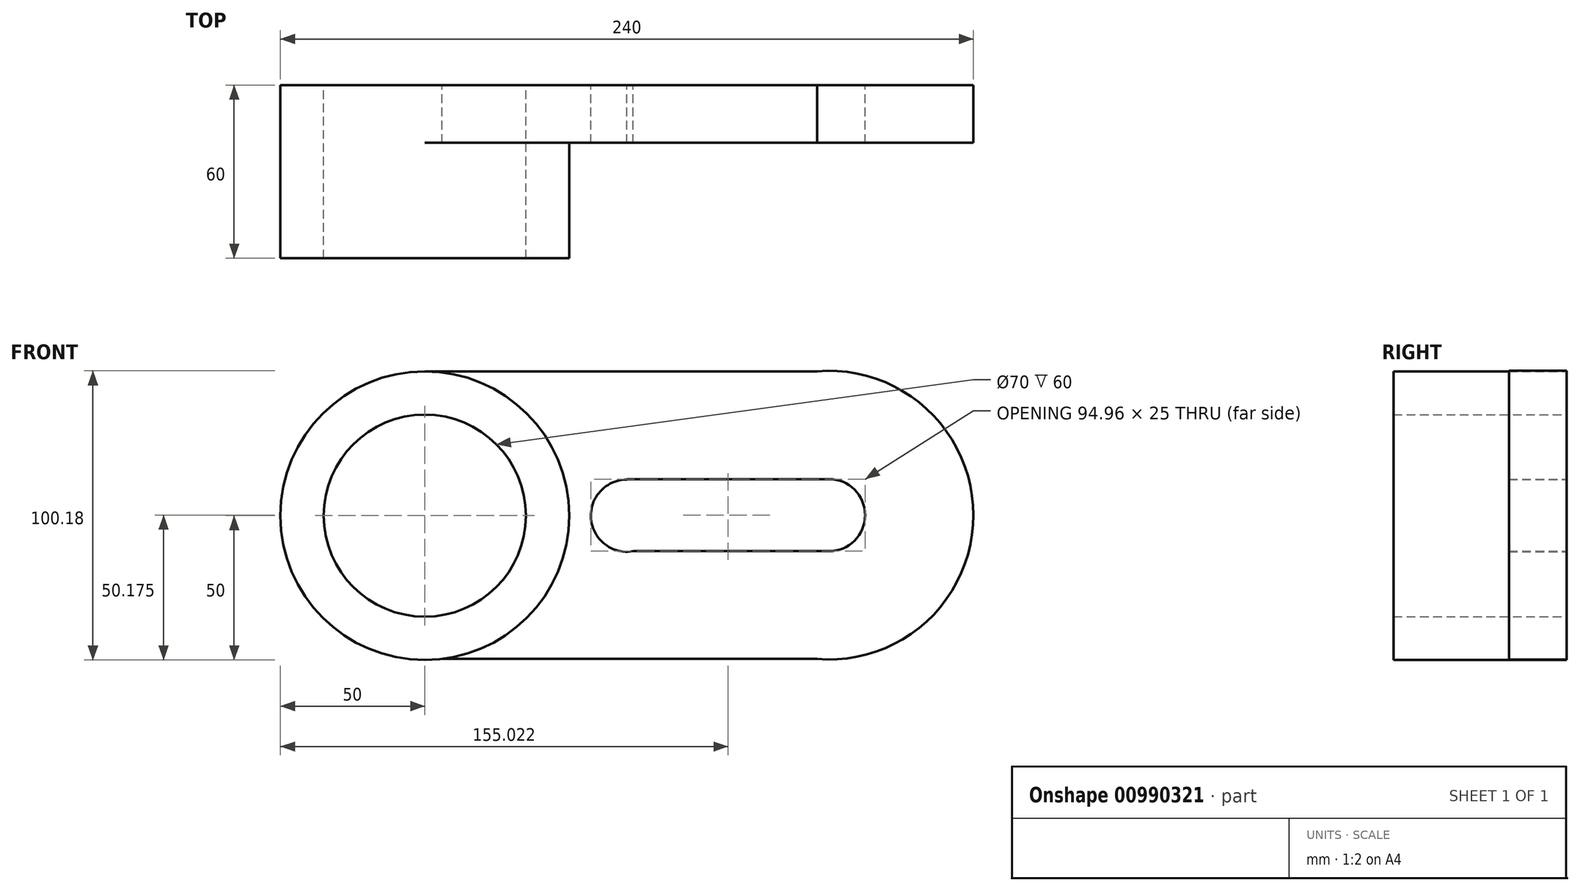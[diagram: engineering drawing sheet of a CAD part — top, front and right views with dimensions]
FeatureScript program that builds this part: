
annotation { "Feature Type Name" : "Feature", "Feature Type Description" : "" }
export const myFeature = defineFeature(function(context is Context, id is Id, definition is map)
    precondition{}
    {
        {
            var Q0;
            Q0=qCreatedBy(makeId("Front.planeOp"),FACE);
            var sketch = newSketch(context, id + "F0", { "sketchPlane" : qUnion([Q0])});
            skCircle(sketch, "E0", {"center": v(0, 0) * mm, "radius": 35 * mm});
            skCircle(sketch, "E1", {"center": v(0, 0) * mm, "radius": 50 * mm});
            skLineSegment(sketch, "E2.bottom", {"start": v(0, 50) * mm, "end": v(140, 50) * mm});
            skLineSegment(sketch, "E2.top", {"start": v(0, -49.65) * mm, "end": v(140, -49.65) * mm});
            skLineSegment(sketch, "E2.left", {"start": v(0, 50) * mm, "end": v(0, -49.65) * mm});
            skLineSegment(sketch, "E2.right", {"start": v(140, 50) * mm, "end": v(140, -49.65) * mm});
            skCircle(sketch, "E3", {"center": v(140, 0.18) * mm, "radius": 50 * mm});
            skCircle(sketch, "E4", {"center": v(140, 0.18) * mm, "radius": 12.5 * mm});
            skLineSegment(sketch, "E5.bottom", {"start": v(140, 12.68) * mm, "end": v(70, 12.68) * mm});
            skLineSegment(sketch, "E5.top", {"start": v(140, -12.32) * mm, "end": v(70, -12.32) * mm});
            skLineSegment(sketch, "E5.left", {"start": v(140, 12.68) * mm, "end": v(140, -12.32) * mm});
            skLineSegment(sketch, "E5.right", {"start": v(70, 12.68) * mm, "end": v(70, -12.32) * mm});
            skCircle(sketch, "E6", {"center": v(70, 0) * mm, "radius": 12.5 * mm});
            skSolve(sketch);
        }
        {
            var Q0;
            Q0=makeQuery(id+"F0.imprint","IMPRINT",FACE,{"disambiguationData":[TD([[makeQuery(id+"F0.imprint","IMPRINT",EDGE,{"derivedFrom":sQuery(id+"F0.wireOp",EDGE,"E0")}),-1.0]])]});
            extrude(context, id + "F1", {"entities" : qUnion([Q0]), "depth" : 60 * mm, "offsetDistance" : 25 * mm});
        }
        {
            var Q0;
            Q0 = qSketchRegion(id + "F0", true);
            extrude(context, id + "F2", {"entities" : qUnion([Q0]), "operationType" : NewBodyOperationType.ADD, "depth" : 20 * mm, "offsetDistance" : 25 * mm});
        }
    });
